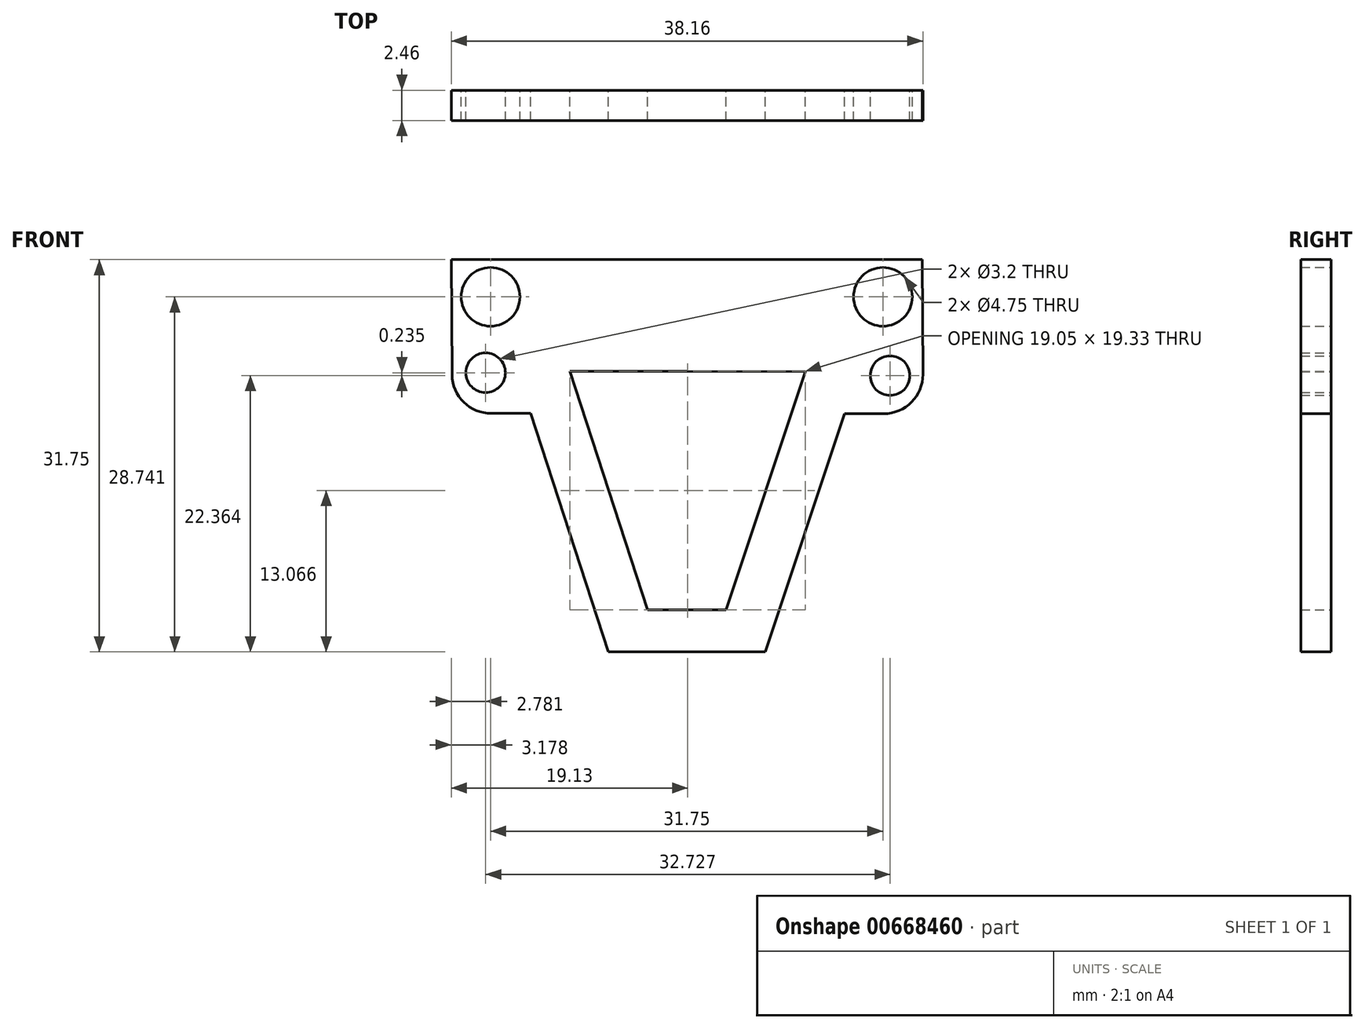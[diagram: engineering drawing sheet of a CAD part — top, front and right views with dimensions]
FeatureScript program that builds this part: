
annotation { "Feature Type Name" : "Feature", "Feature Type Description" : "" }
export const myFeature = defineFeature(function(context is Context, id is Id, definition is map)
    precondition{}
    {
        {
            var Q0;
            Q0=qCreatedBy(makeId("Front.planeOp"),FACE);
            var sketch = newSketch(context, id + "F0", { "sketchPlane" : qUnion([Q0])});
            skLineSegment(sketch, "E0.bottom", {"start": v(-7.3, 27.75) * mm, "end": v(30.8, 27.75) * mm});
            skLineSegment(sketch, "E0.left", {"start": v(-7.3, 27.75) * mm, "end": v(-7.24, 18.2) * mm});
            skLineSegment(sketch, "E0.right", {"start": v(30.8, 27.75) * mm, "end": v(30.86, 18.47) * mm});
            skCircle(sketch, "E1", {"center": v(27.63, 24.74) * mm, "radius": 2.37 * mm});
            skCircle(sketch, "E2.MirrorC", {"center": v(-4.12, 24.74) * mm, "radius": 2.37 * mm});
            skCircle(sketch, "E3", {"center": v(28.2, 18.36) * mm, "radius": 1.6 * mm});
            skCircle(sketch, "E4.MirrorC", {"center": v(-4.52, 18.6) * mm, "radius": 1.6 * mm});
            skPoint(sketch, "E5.visualSharp", {"position": v(30.88, 15.28) * mm});
            skArc(sketch, "E5.filletArc", {"start": v(27.7, 15.28) * mm, "mid": v(29.94, 16.22) * mm, "end": v(30.86, 18.47) * mm});
            skLineSegment(sketch, "E6", {"start": v(24.53, 15.28) * mm, "end": v(27.7, 15.28) * mm});
            skLineSegment(sketch, "E7", {"start": v(11.75, -4) * mm, "end": v(18.1, -4) * mm});
            skLineSegment(sketch, "E8", {"start": v(11.75, -4) * mm, "end": v(5.4, -4) * mm});
            skLineSegment(sketch, "E9", {"start": v(5.4, -4) * mm, "end": v(-0.87, 15.33) * mm});
            skLineSegment(sketch, "E10", {"start": v(18.1, -4) * mm, "end": v(24.53, 15.28) * mm});
            skLineSegment(sketch, "E11", {"start": v(-0.87, 15.33) * mm, "end": v(-4.05, 15.31) * mm});
            skLineSegment(sketch, "E12", {"start": v(-7.24, 18.2) * mm, "end": v(-7.24, 18.46) * mm});
            skPoint(sketch, "E13.visualSharp", {"position": v(-7.22, 15.3) * mm});
            skArc(sketch, "E13.filletArc", {"start": v(-7.24, 18.46) * mm, "mid": v(-6.3, 16.23) * mm, "end": v(-4.05, 15.31) * mm});
            skLineSegment(sketch, "E14", {"start": v(11.75, -0.6) * mm, "end": v(8.58, -0.6) * mm});
            skLineSegment(sketch, "E15", {"start": v(11.75, -0.6) * mm, "end": v(14.93, -0.6) * mm});
            skLineSegment(sketch, "E16", {"start": v(8.58, -0.6) * mm, "end": v(2.3, 18.73) * mm});
            skLineSegment(sketch, "E17", {"start": v(14.93, -0.6) * mm, "end": v(21.35, 18.68) * mm});
            skLineSegment(sketch, "E18", {"start": v(2.3, 18.73) * mm, "end": v(11.75, 18.73) * mm});
            skLineSegment(sketch, "E19", {"start": v(11.75, 18.73) * mm, "end": v(21.35, 18.68) * mm});
            skSolve(sketch);
        }
        {
            var Q0;
            {var subQ0=sQuery(id+"F0.wireOp",EDGE,"E0.bottom");Q0=makeQuery(id+"F0.imprint","IMPRINT",FACE,{"disambiguationData":[TD([[makeQuery(id+"F0.imprint","IMPRINT",EDGE,{"derivedFrom":subQ0}),-1.0]])]});}
            extrude(context, id + "F1", {"entities" : qUnion([Q0]), "depth" : 2.46 * mm});
        }
    });
